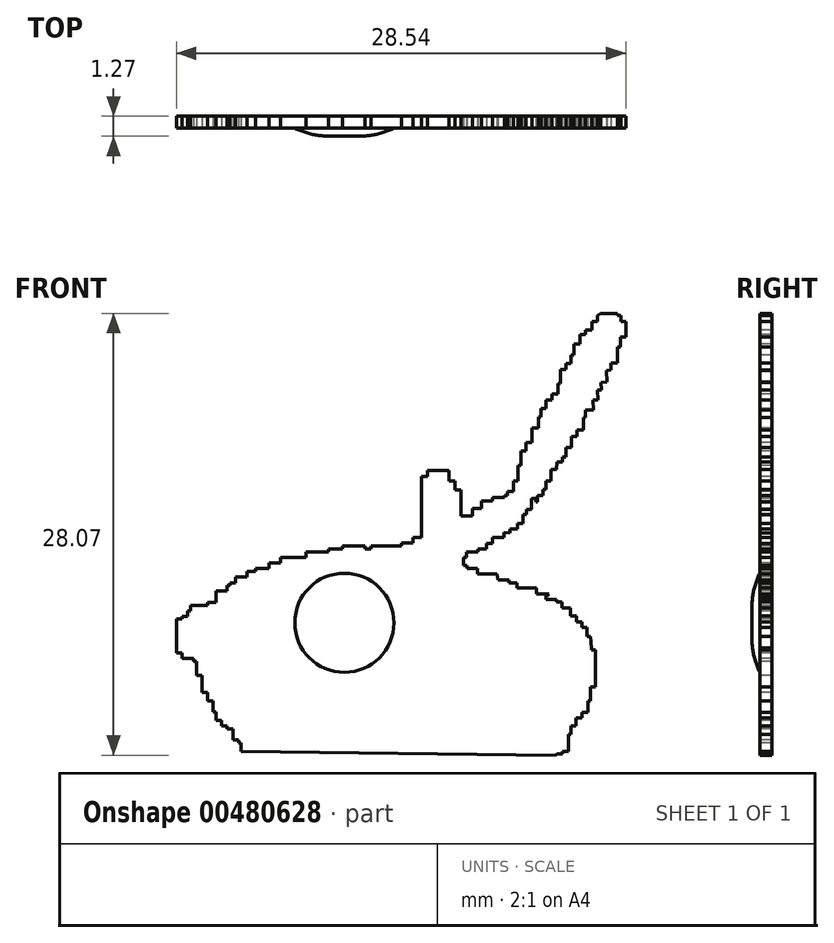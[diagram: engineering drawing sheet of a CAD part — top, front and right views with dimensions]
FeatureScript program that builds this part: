
annotation { "Feature Type Name" : "Feature", "Feature Type Description" : "" }
export const myFeature = defineFeature(function(context is Context, id is Id, definition is map)
    precondition{}
    {
        {
            var Q0;
            Q0=qCreatedBy(makeId("Front.planeOp"),FACE);
            var sketch = newSketch(context, id + "F0", { "sketchPlane" : qUnion([Q0])});
            skLineSegment(sketch, "E0", {"start": v(-10.7, 16.44) * mm, "end": v(-10.7, 16.98) * mm});
            skLineSegment(sketch, "E1", {"start": v(-10.7, 16.98) * mm, "end": v(-10.87, 16.98) * mm});
            skLineSegment(sketch, "E2", {"start": v(-10.87, 16.98) * mm, "end": v(-10.87, 17.16) * mm});
            skLineSegment(sketch, "E3", {"start": v(-10.87, 17.16) * mm, "end": v(-11.22, 17.16) * mm});
            skLineSegment(sketch, "E4", {"start": v(-11.22, 17.16) * mm, "end": v(-11.22, 17.87) * mm});
            skLineSegment(sketch, "E5", {"start": v(-11.22, 17.87) * mm, "end": v(-11.59, 17.87) * mm});
            skLineSegment(sketch, "E6", {"start": v(-11.59, 17.87) * mm, "end": v(-11.59, 18.05) * mm});
            skLineSegment(sketch, "E7", {"start": v(-11.59, 18.05) * mm, "end": v(-11.94, 18.05) * mm});
            skLineSegment(sketch, "E8", {"start": v(-11.94, 18.05) * mm, "end": v(-11.94, 18.4) * mm});
            skLineSegment(sketch, "E9", {"start": v(-11.94, 18.4) * mm, "end": v(-12.3, 18.4) * mm});
            skLineSegment(sketch, "E10", {"start": v(-12.3, 18.4) * mm, "end": v(-12.3, 18.95) * mm});
            skLineSegment(sketch, "E11", {"start": v(-12.3, 18.95) * mm, "end": v(-12.47, 18.95) * mm});
            skLineSegment(sketch, "E12", {"start": v(-12.47, 18.95) * mm, "end": v(-12.47, 19.66) * mm});
            skLineSegment(sketch, "E13", {"start": v(-12.47, 19.66) * mm, "end": v(-12.83, 19.66) * mm});
            skLineSegment(sketch, "E14", {"start": v(-12.83, 19.66) * mm, "end": v(-12.83, 20.2) * mm});
            skLineSegment(sketch, "E15", {"start": v(-12.83, 20.2) * mm, "end": v(-13.2, 20.2) * mm});
            skLineSegment(sketch, "E16", {"start": v(-13.2, 20.2) * mm, "end": v(-13.2, 21.27) * mm});
            skLineSegment(sketch, "E17", {"start": v(-13.2, 21.27) * mm, "end": v(-13.55, 21.27) * mm});
            skLineSegment(sketch, "E18", {"start": v(-13.55, 21.27) * mm, "end": v(-13.55, 22.17) * mm});
            skLineSegment(sketch, "E19", {"start": v(-13.55, 22.17) * mm, "end": v(-13.73, 22.17) * mm});
            skLineSegment(sketch, "E20", {"start": v(-13.73, 22.17) * mm, "end": v(-13.73, 22.35) * mm});
            skLineSegment(sketch, "E21", {"start": v(-13.73, 22.35) * mm, "end": v(-14.44, 22.35) * mm});
            skLineSegment(sketch, "E22", {"start": v(-14.44, 22.35) * mm, "end": v(-14.44, 22.7) * mm});
            skLineSegment(sketch, "E23", {"start": v(-14.44, 22.7) * mm, "end": v(-14.8, 22.7) * mm});
            skLineSegment(sketch, "E24", {"start": v(-14.8, 22.7) * mm, "end": v(-14.8, 24.83) * mm});
            skLineSegment(sketch, "E25", {"start": v(-14.8, 24.83) * mm, "end": v(-14.45, 24.83) * mm});
            skLineSegment(sketch, "E26", {"start": v(-14.45, 24.83) * mm, "end": v(-14.45, 25.02) * mm});
            skLineSegment(sketch, "E27", {"start": v(-14.45, 25.02) * mm, "end": v(-14.1, 25.02) * mm});
            skLineSegment(sketch, "E28", {"start": v(-14.1, 25.02) * mm, "end": v(-14.1, 25.36) * mm});
            skLineSegment(sketch, "E29", {"start": v(-14.1, 25.36) * mm, "end": v(-13.91, 25.36) * mm});
            skLineSegment(sketch, "E30", {"start": v(-13.91, 25.36) * mm, "end": v(-13.91, 25.71) * mm});
            skLineSegment(sketch, "E31", {"start": v(-13.91, 25.71) * mm, "end": v(-12.85, 25.71) * mm});
            skLineSegment(sketch, "E32", {"start": v(-12.85, 25.71) * mm, "end": v(-12.85, 25.9) * mm});
            skLineSegment(sketch, "E33", {"start": v(-12.85, 25.9) * mm, "end": v(-12.3, 25.9) * mm});
            skLineSegment(sketch, "E34", {"start": v(-12.3, 25.9) * mm, "end": v(-12.3, 26.63) * mm});
            skLineSegment(sketch, "E35", {"start": v(-12.3, 26.63) * mm, "end": v(-11.59, 26.63) * mm});
            skLineSegment(sketch, "E36", {"start": v(-11.59, 26.63) * mm, "end": v(-11.59, 26.97) * mm});
            skLineSegment(sketch, "E37", {"start": v(-11.59, 26.97) * mm, "end": v(-11.42, 26.97) * mm});
            skLineSegment(sketch, "E38", {"start": v(-11.42, 26.97) * mm, "end": v(-11.42, 27.15) * mm});
            skLineSegment(sketch, "E39", {"start": v(-11.42, 27.15) * mm, "end": v(-11.05, 27.15) * mm});
            skLineSegment(sketch, "E40", {"start": v(-11.05, 27.15) * mm, "end": v(-11.05, 27.51) * mm});
            skLineSegment(sketch, "E41", {"start": v(-11.05, 27.51) * mm, "end": v(-10.34, 27.51) * mm});
            skLineSegment(sketch, "E42", {"start": v(-10.34, 27.51) * mm, "end": v(-10.34, 27.87) * mm});
            skLineSegment(sketch, "E43", {"start": v(-10.34, 27.87) * mm, "end": v(-9.8, 27.87) * mm});
            skLineSegment(sketch, "E44", {"start": v(-9.8, 27.87) * mm, "end": v(-9.8, 28.06) * mm});
            skLineSegment(sketch, "E45", {"start": v(-9.8, 28.06) * mm, "end": v(-8.92, 28.06) * mm});
            skLineSegment(sketch, "E46", {"start": v(-8.92, 28.06) * mm, "end": v(-8.92, 28.42) * mm});
            skLineSegment(sketch, "E47", {"start": v(-8.92, 28.42) * mm, "end": v(-8.2, 28.42) * mm});
            skLineSegment(sketch, "E48", {"start": v(-8.2, 28.42) * mm, "end": v(-8.2, 28.76) * mm});
            skLineSegment(sketch, "E49", {"start": v(-8.2, 28.76) * mm, "end": v(-6.59, 28.76) * mm});
            skLineSegment(sketch, "E50", {"start": v(-6.59, 28.76) * mm, "end": v(-6.59, 29.12) * mm});
            skLineSegment(sketch, "E51", {"start": v(-6.59, 29.12) * mm, "end": v(-5.15, 29.12) * mm});
            skLineSegment(sketch, "E52", {"start": v(-5.15, 29.12) * mm, "end": v(-5.15, 29.3) * mm});
            skLineSegment(sketch, "E53", {"start": v(-5.15, 29.3) * mm, "end": v(-4.26, 29.3) * mm});
            skLineSegment(sketch, "E54", {"start": v(-4.26, 29.3) * mm, "end": v(-4.26, 29.48) * mm});
            skLineSegment(sketch, "E55", {"start": v(-4.26, 29.48) * mm, "end": v(-2.83, 29.48) * mm});
            skLineSegment(sketch, "E56", {"start": v(-2.83, 29.48) * mm, "end": v(-2.83, 29.3) * mm});
            skLineSegment(sketch, "E57", {"start": v(-2.83, 29.3) * mm, "end": v(-2.47, 29.3) * mm});
            skLineSegment(sketch, "E58", {"start": v(-2.47, 29.3) * mm, "end": v(-2.47, 29.48) * mm});
            skLineSegment(sketch, "E59", {"start": v(-2.47, 29.48) * mm, "end": v(-0.5, 29.48) * mm});
            skLineSegment(sketch, "E60", {"start": v(-0.5, 29.48) * mm, "end": v(-0.5, 29.66) * mm});
            skLineSegment(sketch, "E61", {"start": v(-0.5, 29.66) * mm, "end": v(0.21, 29.66) * mm});
            skLineSegment(sketch, "E62", {"start": v(0.21, 29.66) * mm, "end": v(0.21, 30.01) * mm});
            skLineSegment(sketch, "E63", {"start": v(0.21, 30.01) * mm, "end": v(0.76, 30.01) * mm});
            skLineSegment(sketch, "E64", {"start": v(0.76, 30.01) * mm, "end": v(0.76, 33.9) * mm});
            skLineSegment(sketch, "E65", {"start": v(0.76, 33.9) * mm, "end": v(1.13, 33.9) * mm});
            skLineSegment(sketch, "E66", {"start": v(1.13, 33.9) * mm, "end": v(1.13, 34.27) * mm});
            skLineSegment(sketch, "E67", {"start": v(1.13, 34.27) * mm, "end": v(2.51, 34.27) * mm});
            skLineSegment(sketch, "E68", {"start": v(2.51, 34.27) * mm, "end": v(2.51, 33.61) * mm});
            skLineSegment(sketch, "E69", {"start": v(2.51, 33.61) * mm, "end": v(2.88, 33.61) * mm});
            skLineSegment(sketch, "E70", {"start": v(2.88, 33.61) * mm, "end": v(2.88, 33.05) * mm});
            skLineSegment(sketch, "E71", {"start": v(2.88, 33.05) * mm, "end": v(3.26, 33.05) * mm});
            skLineSegment(sketch, "E72", {"start": v(3.26, 33.05) * mm, "end": v(3.26, 31.39) * mm});
            skLineSegment(sketch, "E73", {"start": v(3.26, 31.39) * mm, "end": v(4, 31.39) * mm});
            skLineSegment(sketch, "E74", {"start": v(4, 31.39) * mm, "end": v(4, 31.85) * mm});
            skLineSegment(sketch, "E75", {"start": v(4, 31.85) * mm, "end": v(4.56, 31.85) * mm});
            skLineSegment(sketch, "E76", {"start": v(4.56, 31.85) * mm, "end": v(4.56, 32.33) * mm});
            skLineSegment(sketch, "E77", {"start": v(4.56, 32.33) * mm, "end": v(5.28, 32.33) * mm});
            skLineSegment(sketch, "E78", {"start": v(5.28, 32.33) * mm, "end": v(5.28, 32.55) * mm});
            skLineSegment(sketch, "E79", {"start": v(5.28, 32.55) * mm, "end": v(6, 32.55) * mm});
            skLineSegment(sketch, "E80", {"start": v(6, 32.55) * mm, "end": v(6, 32.7) * mm});
            skLineSegment(sketch, "E81", {"start": v(6, 32.7) * mm, "end": v(6.22, 32.7) * mm});
            skLineSegment(sketch, "E82", {"start": v(6.22, 32.7) * mm, "end": v(6.22, 32.96) * mm});
            skLineSegment(sketch, "E83", {"start": v(6.22, 32.96) * mm, "end": v(6.6, 32.96) * mm});
            skLineSegment(sketch, "E84", {"start": v(6.6, 32.96) * mm, "end": v(6.6, 33.61) * mm});
            skLineSegment(sketch, "E85", {"start": v(6.6, 33.61) * mm, "end": v(6.88, 33.61) * mm});
            skLineSegment(sketch, "E86", {"start": v(6.88, 33.61) * mm, "end": v(6.88, 34.6) * mm});
            skLineSegment(sketch, "E87", {"start": v(6.88, 34.6) * mm, "end": v(7.09, 34.6) * mm});
            skLineSegment(sketch, "E88", {"start": v(7.09, 34.6) * mm, "end": v(7.09, 35.53) * mm});
            skLineSegment(sketch, "E89", {"start": v(7.09, 35.53) * mm, "end": v(7.4, 35.53) * mm});
            skLineSegment(sketch, "E90", {"start": v(7.4, 35.53) * mm, "end": v(7.4, 36.05) * mm});
            skLineSegment(sketch, "E91", {"start": v(7.4, 36.05) * mm, "end": v(7.77, 36.05) * mm});
            skLineSegment(sketch, "E92", {"start": v(7.77, 36.05) * mm, "end": v(7.77, 36.96) * mm});
            skLineSegment(sketch, "E93", {"start": v(7.77, 36.96) * mm, "end": v(8.18, 36.96) * mm});
            skLineSegment(sketch, "E94", {"start": v(8.18, 36.96) * mm, "end": v(8.18, 37.67) * mm});
            skLineSegment(sketch, "E95", {"start": v(8.18, 37.67) * mm, "end": v(8.34, 37.67) * mm});
            skLineSegment(sketch, "E96", {"start": v(8.34, 37.67) * mm, "end": v(8.34, 38.2) * mm});
            skLineSegment(sketch, "E97", {"start": v(8.34, 38.2) * mm, "end": v(8.66, 38.2) * mm});
            skLineSegment(sketch, "E98", {"start": v(8.66, 38.2) * mm, "end": v(8.66, 38.76) * mm});
            skLineSegment(sketch, "E99", {"start": v(8.66, 38.76) * mm, "end": v(9.04, 38.76) * mm});
            skLineSegment(sketch, "E100", {"start": v(9.04, 38.76) * mm, "end": v(9.04, 39.13) * mm});
            skLineSegment(sketch, "E101", {"start": v(9.04, 39.13) * mm, "end": v(9.42, 39.13) * mm});
            skLineSegment(sketch, "E102", {"start": v(9.42, 39.13) * mm, "end": v(9.42, 39.8) * mm});
            skLineSegment(sketch, "E103", {"start": v(9.42, 39.8) * mm, "end": v(9.57, 39.8) * mm});
            skLineSegment(sketch, "E104", {"start": v(9.57, 39.8) * mm, "end": v(9.57, 40.7) * mm});
            skLineSegment(sketch, "E105", {"start": v(9.57, 40.7) * mm, "end": v(9.94, 40.7) * mm});
            skLineSegment(sketch, "E106", {"start": v(9.94, 40.7) * mm, "end": v(9.94, 41.08) * mm});
            skLineSegment(sketch, "E107", {"start": v(9.94, 41.08) * mm, "end": v(10.24, 41.08) * mm});
            skLineSegment(sketch, "E108", {"start": v(10.24, 41.08) * mm, "end": v(10.24, 41.61) * mm});
            skLineSegment(sketch, "E109", {"start": v(10.24, 41.61) * mm, "end": v(10.45, 41.61) * mm});
            skLineSegment(sketch, "E110", {"start": v(10.45, 41.61) * mm, "end": v(10.45, 42.32) * mm});
            skLineSegment(sketch, "E111", {"start": v(10.45, 42.32) * mm, "end": v(10.8, 42.32) * mm});
            skLineSegment(sketch, "E112", {"start": v(10.8, 42.32) * mm, "end": v(10.8, 42.93) * mm});
            skLineSegment(sketch, "E113", {"start": v(10.8, 42.93) * mm, "end": v(11.17, 42.93) * mm});
            skLineSegment(sketch, "E114", {"start": v(11.17, 42.93) * mm, "end": v(11.17, 43.2) * mm});
            skLineSegment(sketch, "E115", {"start": v(11.17, 43.2) * mm, "end": v(11.59, 43.2) * mm});
            skLineSegment(sketch, "E116", {"start": v(11.59, 43.2) * mm, "end": v(11.59, 43.75) * mm});
            skLineSegment(sketch, "E117", {"start": v(11.59, 43.75) * mm, "end": v(11.92, 43.75) * mm});
            skLineSegment(sketch, "E118", {"start": v(11.92, 43.75) * mm, "end": v(11.92, 44.13) * mm});
            skLineSegment(sketch, "E119", {"start": v(11.92, 44.13) * mm, "end": v(12.13, 44.26) * mm});
            skLineSegment(sketch, "E120", {"start": v(12.13, 44.26) * mm, "end": v(13.19, 44.26) * mm});
            skLineSegment(sketch, "E121", {"start": v(13.19, 44.26) * mm, "end": v(13.19, 44.13) * mm});
            skLineSegment(sketch, "E122", {"start": v(13.19, 44.13) * mm, "end": v(13.41, 44.13) * mm});
            skLineSegment(sketch, "E123", {"start": v(13.41, 44.13) * mm, "end": v(13.41, 43.75) * mm});
            skLineSegment(sketch, "E124", {"start": v(13.41, 43.75) * mm, "end": v(13.73, 43.75) * mm});
            skLineSegment(sketch, "E125", {"start": v(13.73, 43.75) * mm, "end": v(13.73, 42.76) * mm});
            skLineSegment(sketch, "E126", {"start": v(13.73, 42.76) * mm, "end": v(13.4, 42.76) * mm});
            skLineSegment(sketch, "E127", {"start": v(13.4, 42.76) * mm, "end": v(13.4, 42.12) * mm});
            skLineSegment(sketch, "E128", {"start": v(13.4, 42.12) * mm, "end": v(13.19, 42.12) * mm});
            skLineSegment(sketch, "E129", {"start": v(13.19, 42.12) * mm, "end": v(13.19, 41.12) * mm});
            skLineSegment(sketch, "E130", {"start": v(13.19, 41.12) * mm, "end": v(12.8, 41.12) * mm});
            skLineSegment(sketch, "E131", {"start": v(12.8, 41.12) * mm, "end": v(12.8, 40.66) * mm});
            skLineSegment(sketch, "E132", {"start": v(12.8, 40.66) * mm, "end": v(12.5, 40.64) * mm});
            skLineSegment(sketch, "E133", {"start": v(12.5, 40.64) * mm, "end": v(12.54, 39.9) * mm});
            skLineSegment(sketch, "E134", {"start": v(12.54, 39.9) * mm, "end": v(12.16, 39.88) * mm});
            skLineSegment(sketch, "E135", {"start": v(12.16, 39.88) * mm, "end": v(12.18, 39.4) * mm});
            skLineSegment(sketch, "E136", {"start": v(12.18, 39.4) * mm, "end": v(11.92, 39.4) * mm});
            skLineSegment(sketch, "E137", {"start": v(11.92, 39.4) * mm, "end": v(11.95, 38.76) * mm});
            skLineSegment(sketch, "E138", {"start": v(11.95, 38.76) * mm, "end": v(11.64, 38.74) * mm});
            skLineSegment(sketch, "E139", {"start": v(11.64, 38.74) * mm, "end": v(11.67, 38.13) * mm});
            skLineSegment(sketch, "E140", {"start": v(11.67, 38.13) * mm, "end": v(11.17, 38.1) * mm});
            skLineSegment(sketch, "E141", {"start": v(11.17, 38.1) * mm, "end": v(11.17, 37.65) * mm});
            skLineSegment(sketch, "E142", {"start": v(11.17, 37.65) * mm, "end": v(11.05, 37.65) * mm});
            skLineSegment(sketch, "E143", {"start": v(11.05, 37.65) * mm, "end": v(11.05, 37.54) * mm});
            skLineSegment(sketch, "E144", {"start": v(11.05, 37.54) * mm, "end": v(11.05, 36.84) * mm});
            skLineSegment(sketch, "E145", {"start": v(11.05, 36.84) * mm, "end": v(10.63, 36.84) * mm});
            skLineSegment(sketch, "E146", {"start": v(10.63, 36.84) * mm, "end": v(10.63, 36.45) * mm});
            skLineSegment(sketch, "E147", {"start": v(10.63, 36.45) * mm, "end": v(10.27, 36.45) * mm});
            skLineSegment(sketch, "E148", {"start": v(10.27, 36.45) * mm, "end": v(10.27, 35.74) * mm});
            skLineSegment(sketch, "E149", {"start": v(10.27, 35.74) * mm, "end": v(9.93, 35.74) * mm});
            skLineSegment(sketch, "E150", {"start": v(9.93, 35.74) * mm, "end": v(9.93, 35.14) * mm});
            skLineSegment(sketch, "E151", {"start": v(9.93, 35.14) * mm, "end": v(9.72, 35.14) * mm});
            skLineSegment(sketch, "E152", {"start": v(9.72, 35.14) * mm, "end": v(9.72, 34.83) * mm});
            skLineSegment(sketch, "E153", {"start": v(9.72, 34.83) * mm, "end": v(9.36, 34.83) * mm});
            skLineSegment(sketch, "E154", {"start": v(9.36, 34.83) * mm, "end": v(9.33, 34.33) * mm});
            skLineSegment(sketch, "E155", {"start": v(9.33, 34.33) * mm, "end": v(8.98, 34.33) * mm});
            skLineSegment(sketch, "E156", {"start": v(8.98, 34.33) * mm, "end": v(8.98, 33.6) * mm});
            skLineSegment(sketch, "E157", {"start": v(8.98, 33.6) * mm, "end": v(8.65, 33.6) * mm});
            skLineSegment(sketch, "E158", {"start": v(8.65, 33.6) * mm, "end": v(8.65, 33.07) * mm});
            skLineSegment(sketch, "E159", {"start": v(8.65, 33.07) * mm, "end": v(8.46, 33.07) * mm});
            skLineSegment(sketch, "E160", {"start": v(8.46, 33.07) * mm, "end": v(8.46, 32.7) * mm});
            skLineSegment(sketch, "E161", {"start": v(8.46, 32.7) * mm, "end": v(8.1, 32.7) * mm});
            skLineSegment(sketch, "E162", {"start": v(8.1, 32.7) * mm, "end": v(8.1, 32.28) * mm});
            skLineSegment(sketch, "E163", {"start": v(8.1, 32.28) * mm, "end": v(8.02, 32.28) * mm});
            skLineSegment(sketch, "E164", {"start": v(8.02, 32.28) * mm, "end": v(8.02, 32.51) * mm});
            skLineSegment(sketch, "E165", {"start": v(8.02, 32.51) * mm, "end": v(7.73, 32.51) * mm});
            skLineSegment(sketch, "E166", {"start": v(7.73, 32.51) * mm, "end": v(7.73, 31.8) * mm});
            skLineSegment(sketch, "E167", {"start": v(7.73, 31.8) * mm, "end": v(7.41, 31.8) * mm});
            skLineSegment(sketch, "E168", {"start": v(7.41, 31.8) * mm, "end": v(7.41, 31.47) * mm});
            skLineSegment(sketch, "E169", {"start": v(7.41, 31.47) * mm, "end": v(7.21, 31.47) * mm});
            skLineSegment(sketch, "E170", {"start": v(7.21, 31.47) * mm, "end": v(7.21, 30.92) * mm});
            skLineSegment(sketch, "E171", {"start": v(7.21, 30.92) * mm, "end": v(6.85, 30.92) * mm});
            skLineSegment(sketch, "E172", {"start": v(6.85, 30.92) * mm, "end": v(6.85, 30.58) * mm});
            skLineSegment(sketch, "E173", {"start": v(6.85, 30.58) * mm, "end": v(6.36, 30.58) * mm});
            skLineSegment(sketch, "E174", {"start": v(6.36, 30.58) * mm, "end": v(6.36, 30.3) * mm});
            skLineSegment(sketch, "E175", {"start": v(6.36, 30.3) * mm, "end": v(6, 30.36) * mm});
            skLineSegment(sketch, "E176", {"start": v(6, 30.36) * mm, "end": v(6, 30.02) * mm});
            skLineSegment(sketch, "E177", {"start": v(6, 30.02) * mm, "end": v(5.28, 30.02) * mm});
            skLineSegment(sketch, "E178", {"start": v(5.28, 30.02) * mm, "end": v(5.28, 29.63) * mm});
            skLineSegment(sketch, "E179", {"start": v(5.28, 29.63) * mm, "end": v(4.88, 29.63) * mm});
            skLineSegment(sketch, "E180", {"start": v(4.88, 29.63) * mm, "end": v(4.88, 29.3) * mm});
            skLineSegment(sketch, "E181", {"start": v(4.88, 29.3) * mm, "end": v(4.34, 29.3) * mm});
            skLineSegment(sketch, "E182", {"start": v(4.34, 29.3) * mm, "end": v(4.34, 29.1) * mm});
            skLineSegment(sketch, "E183", {"start": v(4.34, 29.1) * mm, "end": v(3.6, 29.1) * mm});
            skLineSegment(sketch, "E184", {"start": v(3.6, 29.1) * mm, "end": v(3.6, 28.76) * mm});
            skLineSegment(sketch, "E185", {"start": v(3.6, 28.76) * mm, "end": v(3.4, 28.76) * mm});
            skLineSegment(sketch, "E186", {"start": v(3.4, 28.76) * mm, "end": v(3.4, 28.24) * mm});
            skLineSegment(sketch, "E187", {"start": v(3.4, 28.24) * mm, "end": v(3.63, 28.24) * mm});
            skLineSegment(sketch, "E188", {"start": v(3.63, 28.24) * mm, "end": v(3.63, 28.05) * mm});
            skLineSegment(sketch, "E189", {"start": v(3.63, 28.05) * mm, "end": v(4.32, 28.05) * mm});
            skLineSegment(sketch, "E190", {"start": v(4.32, 28.05) * mm, "end": v(4.32, 27.7) * mm});
            skLineSegment(sketch, "E191", {"start": v(4.32, 27.7) * mm, "end": v(5.56, 27.7) * mm});
            skLineSegment(sketch, "E192", {"start": v(5.56, 27.7) * mm, "end": v(5.62, 27.32) * mm});
            skLineSegment(sketch, "E193", {"start": v(5.62, 27.32) * mm, "end": v(6.32, 27.32) * mm});
            skLineSegment(sketch, "E194", {"start": v(6.32, 27.32) * mm, "end": v(6.32, 27.13) * mm});
            skLineSegment(sketch, "E195", {"start": v(6.32, 27.13) * mm, "end": v(6.81, 27.13) * mm});
            skLineSegment(sketch, "E196", {"start": v(6.81, 27.13) * mm, "end": v(6.81, 26.83) * mm});
            skLineSegment(sketch, "E197", {"start": v(6.81, 26.83) * mm, "end": v(8.05, 26.83) * mm});
            skLineSegment(sketch, "E198", {"start": v(8.05, 26.83) * mm, "end": v(8.05, 26.44) * mm});
            skLineSegment(sketch, "E199", {"start": v(8.05, 26.44) * mm, "end": v(8.84, 26.44) * mm});
            skLineSegment(sketch, "E200", {"start": v(8.84, 26.44) * mm, "end": v(8.76, 26.3) * mm});
            skLineSegment(sketch, "E201", {"start": v(8.76, 26.3) * mm, "end": v(8.66, 26.3) * mm});
            skLineSegment(sketch, "E202", {"start": v(8.66, 26.3) * mm, "end": v(8.66, 26.1) * mm});
            skLineSegment(sketch, "E203", {"start": v(8.66, 26.1) * mm, "end": v(9.33, 26.1) * mm});
            skLineSegment(sketch, "E204", {"start": v(9.33, 26.1) * mm, "end": v(9.33, 25.93) * mm});
            skLineSegment(sketch, "E205", {"start": v(9.33, 25.93) * mm, "end": v(9.69, 25.93) * mm});
            skLineSegment(sketch, "E206", {"start": v(9.69, 25.93) * mm, "end": v(9.69, 25.55) * mm});
            skLineSegment(sketch, "E207", {"start": v(9.69, 25.55) * mm, "end": v(10.22, 25.55) * mm});
            skLineSegment(sketch, "E208", {"start": v(10.22, 25.55) * mm, "end": v(10.22, 25.05) * mm});
            skLineSegment(sketch, "E209", {"start": v(10.22, 25.05) * mm, "end": v(10.58, 25.05) * mm});
            skLineSegment(sketch, "E210", {"start": v(10.58, 25.05) * mm, "end": v(10.58, 24.67) * mm});
            skLineSegment(sketch, "E211", {"start": v(10.58, 24.67) * mm, "end": v(10.93, 24.67) * mm});
            skLineSegment(sketch, "E212", {"start": v(10.93, 24.67) * mm, "end": v(10.93, 24.3) * mm});
            skLineSegment(sketch, "E213", {"start": v(10.93, 24.3) * mm, "end": v(11.28, 24.3) * mm});
            skLineSegment(sketch, "E214", {"start": v(11.28, 24.3) * mm, "end": v(11.28, 23.75) * mm});
            skLineSegment(sketch, "E215", {"start": v(11.28, 23.75) * mm, "end": v(11.49, 23.75) * mm});
            skLineSegment(sketch, "E216", {"start": v(11.49, 23.75) * mm, "end": v(11.56, 23.02) * mm});
            skLineSegment(sketch, "E217", {"start": v(11.56, 23.02) * mm, "end": v(11.56, 22.87) * mm});
            skLineSegment(sketch, "E218", {"start": v(11.56, 22.87) * mm, "end": v(11.8, 22.87) * mm});
            skLineSegment(sketch, "E219", {"start": v(11.8, 22.87) * mm, "end": v(11.8, 20.55) * mm});
            skLineSegment(sketch, "E220", {"start": v(11.8, 20.55) * mm, "end": v(11.48, 20.55) * mm});
            skLineSegment(sketch, "E221", {"start": v(11.48, 20.55) * mm, "end": v(11.48, 19.65) * mm});
            skLineSegment(sketch, "E222", {"start": v(11.48, 19.65) * mm, "end": v(11.32, 19.65) * mm});
            skLineSegment(sketch, "E223", {"start": v(11.32, 19.65) * mm, "end": v(11.32, 18.92) * mm});
            skLineSegment(sketch, "E224", {"start": v(11.32, 18.92) * mm, "end": v(10.95, 18.92) * mm});
            skLineSegment(sketch, "E225", {"start": v(10.95, 18.92) * mm, "end": v(10.95, 18.57) * mm});
            skLineSegment(sketch, "E226", {"start": v(10.95, 18.57) * mm, "end": v(10.58, 18.57) * mm});
            skLineSegment(sketch, "E227", {"start": v(10.58, 18.57) * mm, "end": v(10.58, 18.06) * mm});
            skLineSegment(sketch, "E228", {"start": v(10.58, 18.06) * mm, "end": v(10.26, 18.06) * mm});
            skLineSegment(sketch, "E229", {"start": v(10.26, 18.06) * mm, "end": v(10.26, 17.5) * mm});
            skLineSegment(sketch, "E230", {"start": v(10.26, 17.5) * mm, "end": v(10.08, 17.5) * mm});
            skLineSegment(sketch, "E231", {"start": v(10.08, 17.5) * mm, "end": v(10.08, 16.43) * mm});
            skLineSegment(sketch, "E232", {"start": v(10.08, 16.43) * mm, "end": v(9.71, 16.43) * mm});
            skLineSegment(sketch, "E233", {"start": v(9.71, 16.43) * mm, "end": v(9.71, 16.27) * mm});
            skLineSegment(sketch, "E234", {"start": v(9.71, 16.27) * mm, "end": v(9.36, 16.27) * mm});
            skLineSegment(sketch, "E235", {"start": v(9.36, 16.27) * mm, "end": v(9.27, 16.19) * mm});
            skLineSegment(sketch, "E236", {"start": v(9.27, 16.19) * mm, "end": v(-10.7, 16.44) * mm});
            skSolve(sketch);
        }
        {
            var Q0;
            Q0 = qSketchRegion(id + "F0", true);
            extrude(context, id + "F1", {"entities" : qUnion([Q0]), "oppositeDirection" : true, "depth" : 0.76 * mm});
        }
        {
            var Q0;
            Q0=makeQuery(id+"F1.opExtrude","CAP_FACE",FACE,{"disambiguationData":[OSD([sQuery(id+"F0.wireOp",EDGE,"E0"),sQuery(id+"F0.wireOp",EDGE,"E1"),sQuery(id+"F0.wireOp",EDGE,"E2"),sQuery(id+"F0.wireOp",EDGE,"E3"),sQuery(id+"F0.wireOp",EDGE,"E4"),sQuery(id+"F0.wireOp",EDGE,"E5"),sQuery(id+"F0.wireOp",EDGE,"E6"),sQuery(id+"F0.wireOp",EDGE,"E7"),sQuery(id+"F0.wireOp",EDGE,"E8"),sQuery(id+"F0.wireOp",EDGE,"E9"),sQuery(id+"F0.wireOp",EDGE,"E10"),sQuery(id+"F0.wireOp",EDGE,"E11"),sQuery(id+"F0.wireOp",EDGE,"E12"),sQuery(id+"F0.wireOp",EDGE,"E13"),sQuery(id+"F0.wireOp",EDGE,"E14"),sQuery(id+"F0.wireOp",EDGE,"E15"),sQuery(id+"F0.wireOp",EDGE,"E16"),sQuery(id+"F0.wireOp",EDGE,"E17"),sQuery(id+"F0.wireOp",EDGE,"E18"),sQuery(id+"F0.wireOp",EDGE,"E19"),sQuery(id+"F0.wireOp",EDGE,"E20"),sQuery(id+"F0.wireOp",EDGE,"E21"),sQuery(id+"F0.wireOp",EDGE,"E22"),sQuery(id+"F0.wireOp",EDGE,"E23"),sQuery(id+"F0.wireOp",EDGE,"E24"),sQuery(id+"F0.wireOp",EDGE,"E25"),sQuery(id+"F0.wireOp",EDGE,"E26"),sQuery(id+"F0.wireOp",EDGE,"E27"),sQuery(id+"F0.wireOp",EDGE,"E28"),sQuery(id+"F0.wireOp",EDGE,"E29"),sQuery(id+"F0.wireOp",EDGE,"E30"),sQuery(id+"F0.wireOp",EDGE,"E31"),sQuery(id+"F0.wireOp",EDGE,"E32"),sQuery(id+"F0.wireOp",EDGE,"E33"),sQuery(id+"F0.wireOp",EDGE,"E34"),sQuery(id+"F0.wireOp",EDGE,"E35"),sQuery(id+"F0.wireOp",EDGE,"E36"),sQuery(id+"F0.wireOp",EDGE,"E37"),sQuery(id+"F0.wireOp",EDGE,"E38"),sQuery(id+"F0.wireOp",EDGE,"E39"),sQuery(id+"F0.wireOp",EDGE,"E40"),sQuery(id+"F0.wireOp",EDGE,"E41"),sQuery(id+"F0.wireOp",EDGE,"E42"),sQuery(id+"F0.wireOp",EDGE,"E43"),sQuery(id+"F0.wireOp",EDGE,"E44"),sQuery(id+"F0.wireOp",EDGE,"E45"),sQuery(id+"F0.wireOp",EDGE,"E46"),sQuery(id+"F0.wireOp",EDGE,"E47"),sQuery(id+"F0.wireOp",EDGE,"E48"),sQuery(id+"F0.wireOp",EDGE,"E49"),sQuery(id+"F0.wireOp",EDGE,"E50"),sQuery(id+"F0.wireOp",EDGE,"E51"),sQuery(id+"F0.wireOp",EDGE,"E52"),sQuery(id+"F0.wireOp",EDGE,"E53"),sQuery(id+"F0.wireOp",EDGE,"E54"),sQuery(id+"F0.wireOp",EDGE,"E55"),sQuery(id+"F0.wireOp",EDGE,"E56"),sQuery(id+"F0.wireOp",EDGE,"E57"),sQuery(id+"F0.wireOp",EDGE,"E58"),sQuery(id+"F0.wireOp",EDGE,"E59"),sQuery(id+"F0.wireOp",EDGE,"E60"),sQuery(id+"F0.wireOp",EDGE,"E61"),sQuery(id+"F0.wireOp",EDGE,"E62"),sQuery(id+"F0.wireOp",EDGE,"E63"),sQuery(id+"F0.wireOp",EDGE,"E64"),sQuery(id+"F0.wireOp",EDGE,"E65"),sQuery(id+"F0.wireOp",EDGE,"E66"),sQuery(id+"F0.wireOp",EDGE,"E67"),sQuery(id+"F0.wireOp",EDGE,"E68"),sQuery(id+"F0.wireOp",EDGE,"E69"),sQuery(id+"F0.wireOp",EDGE,"E70"),sQuery(id+"F0.wireOp",EDGE,"E71"),sQuery(id+"F0.wireOp",EDGE,"E72"),sQuery(id+"F0.wireOp",EDGE,"E73"),sQuery(id+"F0.wireOp",EDGE,"E74"),sQuery(id+"F0.wireOp",EDGE,"E75"),sQuery(id+"F0.wireOp",EDGE,"E76"),sQuery(id+"F0.wireOp",EDGE,"E77"),sQuery(id+"F0.wireOp",EDGE,"E78"),sQuery(id+"F0.wireOp",EDGE,"E79"),sQuery(id+"F0.wireOp",EDGE,"E80"),sQuery(id+"F0.wireOp",EDGE,"E81"),sQuery(id+"F0.wireOp",EDGE,"E82"),sQuery(id+"F0.wireOp",EDGE,"E83"),sQuery(id+"F0.wireOp",EDGE,"E84"),sQuery(id+"F0.wireOp",EDGE,"E85"),sQuery(id+"F0.wireOp",EDGE,"E86"),sQuery(id+"F0.wireOp",EDGE,"E87"),sQuery(id+"F0.wireOp",EDGE,"E88"),sQuery(id+"F0.wireOp",EDGE,"E89"),sQuery(id+"F0.wireOp",EDGE,"E90"),sQuery(id+"F0.wireOp",EDGE,"E91"),sQuery(id+"F0.wireOp",EDGE,"E92"),sQuery(id+"F0.wireOp",EDGE,"E93"),sQuery(id+"F0.wireOp",EDGE,"E94"),sQuery(id+"F0.wireOp",EDGE,"E95"),sQuery(id+"F0.wireOp",EDGE,"E96"),sQuery(id+"F0.wireOp",EDGE,"E97"),sQuery(id+"F0.wireOp",EDGE,"E98"),sQuery(id+"F0.wireOp",EDGE,"E99"),sQuery(id+"F0.wireOp",EDGE,"E100"),sQuery(id+"F0.wireOp",EDGE,"E101"),sQuery(id+"F0.wireOp",EDGE,"E102"),sQuery(id+"F0.wireOp",EDGE,"E103"),sQuery(id+"F0.wireOp",EDGE,"E104"),sQuery(id+"F0.wireOp",EDGE,"E105"),sQuery(id+"F0.wireOp",EDGE,"E106"),sQuery(id+"F0.wireOp",EDGE,"E107"),sQuery(id+"F0.wireOp",EDGE,"E108"),sQuery(id+"F0.wireOp",EDGE,"E109"),sQuery(id+"F0.wireOp",EDGE,"E110"),sQuery(id+"F0.wireOp",EDGE,"E111"),sQuery(id+"F0.wireOp",EDGE,"E112"),sQuery(id+"F0.wireOp",EDGE,"E113"),sQuery(id+"F0.wireOp",EDGE,"E114"),sQuery(id+"F0.wireOp",EDGE,"E115"),sQuery(id+"F0.wireOp",EDGE,"E116"),sQuery(id+"F0.wireOp",EDGE,"E117"),sQuery(id+"F0.wireOp",EDGE,"E118"),sQuery(id+"F0.wireOp",EDGE,"E119"),sQuery(id+"F0.wireOp",EDGE,"E120"),sQuery(id+"F0.wireOp",EDGE,"E121"),sQuery(id+"F0.wireOp",EDGE,"E122"),sQuery(id+"F0.wireOp",EDGE,"E123"),sQuery(id+"F0.wireOp",EDGE,"E124"),sQuery(id+"F0.wireOp",EDGE,"E125"),sQuery(id+"F0.wireOp",EDGE,"E126"),sQuery(id+"F0.wireOp",EDGE,"E127"),sQuery(id+"F0.wireOp",EDGE,"E128"),sQuery(id+"F0.wireOp",EDGE,"E129"),sQuery(id+"F0.wireOp",EDGE,"E130"),sQuery(id+"F0.wireOp",EDGE,"E131"),sQuery(id+"F0.wireOp",EDGE,"E132"),sQuery(id+"F0.wireOp",EDGE,"E133"),sQuery(id+"F0.wireOp",EDGE,"E134"),sQuery(id+"F0.wireOp",EDGE,"E135"),sQuery(id+"F0.wireOp",EDGE,"E136"),sQuery(id+"F0.wireOp",EDGE,"E137"),sQuery(id+"F0.wireOp",EDGE,"E138"),sQuery(id+"F0.wireOp",EDGE,"E139"),sQuery(id+"F0.wireOp",EDGE,"E140"),sQuery(id+"F0.wireOp",EDGE,"E141"),sQuery(id+"F0.wireOp",EDGE,"E142"),sQuery(id+"F0.wireOp",EDGE,"E143"),sQuery(id+"F0.wireOp",EDGE,"E144"),sQuery(id+"F0.wireOp",EDGE,"E145"),sQuery(id+"F0.wireOp",EDGE,"E146"),sQuery(id+"F0.wireOp",EDGE,"E147"),sQuery(id+"F0.wireOp",EDGE,"E148"),sQuery(id+"F0.wireOp",EDGE,"E149"),sQuery(id+"F0.wireOp",EDGE,"E150"),sQuery(id+"F0.wireOp",EDGE,"E151"),sQuery(id+"F0.wireOp",EDGE,"E152"),sQuery(id+"F0.wireOp",EDGE,"E153"),sQuery(id+"F0.wireOp",EDGE,"E154"),sQuery(id+"F0.wireOp",EDGE,"E155"),sQuery(id+"F0.wireOp",EDGE,"E156"),sQuery(id+"F0.wireOp",EDGE,"E157"),sQuery(id+"F0.wireOp",EDGE,"E158"),sQuery(id+"F0.wireOp",EDGE,"E159"),sQuery(id+"F0.wireOp",EDGE,"E160"),sQuery(id+"F0.wireOp",EDGE,"E161"),sQuery(id+"F0.wireOp",EDGE,"E162"),sQuery(id+"F0.wireOp",EDGE,"E163"),sQuery(id+"F0.wireOp",EDGE,"E164"),sQuery(id+"F0.wireOp",EDGE,"E165"),sQuery(id+"F0.wireOp",EDGE,"E166"),sQuery(id+"F0.wireOp",EDGE,"E167"),sQuery(id+"F0.wireOp",EDGE,"E168"),sQuery(id+"F0.wireOp",EDGE,"E169"),sQuery(id+"F0.wireOp",EDGE,"E170"),sQuery(id+"F0.wireOp",EDGE,"E171"),sQuery(id+"F0.wireOp",EDGE,"E172"),sQuery(id+"F0.wireOp",EDGE,"E173"),sQuery(id+"F0.wireOp",EDGE,"E174"),sQuery(id+"F0.wireOp",EDGE,"E175"),sQuery(id+"F0.wireOp",EDGE,"E176"),sQuery(id+"F0.wireOp",EDGE,"E177"),sQuery(id+"F0.wireOp",EDGE,"E178"),sQuery(id+"F0.wireOp",EDGE,"E179"),sQuery(id+"F0.wireOp",EDGE,"E180"),sQuery(id+"F0.wireOp",EDGE,"E181"),sQuery(id+"F0.wireOp",EDGE,"E182"),sQuery(id+"F0.wireOp",EDGE,"E183"),sQuery(id+"F0.wireOp",EDGE,"E184"),sQuery(id+"F0.wireOp",EDGE,"E185"),sQuery(id+"F0.wireOp",EDGE,"E186"),sQuery(id+"F0.wireOp",EDGE,"E187"),sQuery(id+"F0.wireOp",EDGE,"E188"),sQuery(id+"F0.wireOp",EDGE,"E189"),sQuery(id+"F0.wireOp",EDGE,"E190"),sQuery(id+"F0.wireOp",EDGE,"E191"),sQuery(id+"F0.wireOp",EDGE,"E192"),sQuery(id+"F0.wireOp",EDGE,"E193"),sQuery(id+"F0.wireOp",EDGE,"E194"),sQuery(id+"F0.wireOp",EDGE,"E195"),sQuery(id+"F0.wireOp",EDGE,"E196"),sQuery(id+"F0.wireOp",EDGE,"E197"),sQuery(id+"F0.wireOp",EDGE,"E198"),sQuery(id+"F0.wireOp",EDGE,"E199"),sQuery(id+"F0.wireOp",EDGE,"E200"),sQuery(id+"F0.wireOp",EDGE,"E201"),sQuery(id+"F0.wireOp",EDGE,"E202"),sQuery(id+"F0.wireOp",EDGE,"E203"),sQuery(id+"F0.wireOp",EDGE,"E204"),sQuery(id+"F0.wireOp",EDGE,"E205"),sQuery(id+"F0.wireOp",EDGE,"E206"),sQuery(id+"F0.wireOp",EDGE,"E207"),sQuery(id+"F0.wireOp",EDGE,"E208"),sQuery(id+"F0.wireOp",EDGE,"E209"),sQuery(id+"F0.wireOp",EDGE,"E210"),sQuery(id+"F0.wireOp",EDGE,"E211"),sQuery(id+"F0.wireOp",EDGE,"E212"),sQuery(id+"F0.wireOp",EDGE,"E213"),sQuery(id+"F0.wireOp",EDGE,"E214"),sQuery(id+"F0.wireOp",EDGE,"E215"),sQuery(id+"F0.wireOp",EDGE,"E216"),sQuery(id+"F0.wireOp",EDGE,"E217"),sQuery(id+"F0.wireOp",EDGE,"E218"),sQuery(id+"F0.wireOp",EDGE,"E219"),sQuery(id+"F0.wireOp",EDGE,"E220"),sQuery(id+"F0.wireOp",EDGE,"E221"),sQuery(id+"F0.wireOp",EDGE,"E222"),sQuery(id+"F0.wireOp",EDGE,"E223"),sQuery(id+"F0.wireOp",EDGE,"E224"),sQuery(id+"F0.wireOp",EDGE,"E225"),sQuery(id+"F0.wireOp",EDGE,"E226"),sQuery(id+"F0.wireOp",EDGE,"E227"),sQuery(id+"F0.wireOp",EDGE,"E228"),sQuery(id+"F0.wireOp",EDGE,"E229"),sQuery(id+"F0.wireOp",EDGE,"E230"),sQuery(id+"F0.wireOp",EDGE,"E231"),sQuery(id+"F0.wireOp",EDGE,"E232"),sQuery(id+"F0.wireOp",EDGE,"E233"),sQuery(id+"F0.wireOp",EDGE,"E234"),sQuery(id+"F0.wireOp",EDGE,"E235"),sQuery(id+"F0.wireOp",EDGE,"E236")])],"isStart":true});
            var sketch = newSketch(context, id + "F2", { "sketchPlane" : qUnion([Q0])});
            skCircle(sketch, "E237", {"center": v(-4.15, 24.6) * mm, "radius": 3.15 * mm});
            skSolve(sketch);
        }
        {
            var Q0;
            Q0 = qSketchRegion(id + "F2", true);
            extrude(context, id + "F3", {"entities" : qUnion([Q0]), "operationType" : NewBodyOperationType.ADD, "depth" : 0.5 * mm});
        }
        {
            var Q0;
            Q0=makeQuery(id+"F3.opExtrude","CAP_EDGE",EDGE,{"disambiguationData":[OSD([sQuery(id+"F2.wireOp",EDGE,"E237")])],"isStart":false});
            fillet(context, id + "F4", {"entities" : qUnion([Q0]), "radius" : 5.08 * mm, "tangentPropagation" : true, "allowEdgeOverflow" : false});
        }
    });
